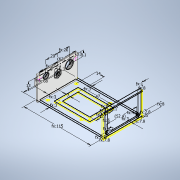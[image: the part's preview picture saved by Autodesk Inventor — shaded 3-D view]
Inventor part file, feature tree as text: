
AUTODESK INVENTOR PART (.ipt)
format: ipt  version: 2022 (Build 260153000, 153)  size: 863,744 bytes
history: native  units: mm
features: extrude x19, sketch x19, fillet x6, plane x4, projected_geometry x4, other x3, revolve x3, pattern_linear x1, mirror x1
ambient origin geometry x8: Origin, YZ Plane, XZ Plane, XY Plane, X Axis, Y Axis, Z Axis, Center Point
bodies: Solid1 (feature_tree)
feature tree (60):
  other  "pi_base_plane"
  extrude  "Extrusion1"  Depth=68.0mm
  extrude  "Extrusion2"  Depth=3.0mm
  other  "pi_outline"
  sketch  "Sketch4"  dims[d2=3.0mm d3=3.0mm]
  extrude  "Extrusion3"  Depth=3.0mm
  sketch  "Sketch5"  dims[d4=3.0mm d5=3.0mm]
  plane  "Work Plane1"
  revolve  "Revolution1"  [1 undecoded]
  sketch  "Sketch Driven Pattern1"  dims[d0=115.0mm d1=68.0mm]
  other  "door"
  extrude  "door_cut"  TaperAngle=0.0deg  [1 undecoded]
  extrude  "Extrusion5"  Depth=85.0mm
  sketch  "Sketch8"  dims[d8=38.0mm d9=0.0mm]
  plane  "Work Plane2"
  extrude  "Extrusion6"  Depth=3.5mm
  revolve  "Revolution2"  [1 undecoded]
  plane  "Work Plane3"
  revolve  "Revolution3"  [1 undecoded]
  fillet  "Fillet1"  Radius=2.7mm
  fillet  "Fillet2"  Radius=3.5mm
  extrude  "Extrusion7"  Depth=2.7mm
  extrude  "M2.5 Side Fastners"  Depth=58.0mm
  sketch  "Sketch14"  dims[d20=58.0mm d21=2.7mm]
  extrude  "Connector and Mount Holes"  Depth=3.0mm
  extrude  "Captive M6 Nut Indent"  Depth=6.5mm
  extrude  "Extrusion12"  Depth=6.5mm
  fillet  "Fillet3"  Radius=6.5mm
  sketch  "Sketch16"  dims[d24=62.0mm d25=3.0mm]
  extrude  "Extrusion13"  TaperAngle=0.0deg  [1 undecoded]
  extrude  "Extrusion14"  Depth=2.1mm
  extrude  "Extrusion15"  TaperAngle=90.0deg  [1 undecoded]
  extrude  "Extrusion16"  Depth=8.0mm
  fillet  "Fillet4"  Radius=8.0mm
  sketch  "Sketch19"  dims[d31=0.4mm d32=0.0mm]
  extrude  "Extrusion17"  Depth=5.0mm
  pattern_linear  "Rectangular Pattern1"  Spacing1=3.0mm  [1 undecoded]
  plane  "Work Plane4"
  mirror  "Mirror1"
  fillet  "Fillet5"  [1 undecoded]
  extrude  "Extrusion18"  Depth=2.0mm TaperAngle=0.0deg
  fillet  "Fillet6"  Radius=4.2mm
  extrude  "Extrusion19"  Depth=7.8mm
  extrude  "Extrusion20"  Depth=7.8mm
  projected_geometry  "Projected Loop1"
  sketch  "Sketch6"  dims[d6=3.0mm d7=0.0mm]
  sketch  "Sketch9"  dims[d10=56.0mm d11=85.0mm]
  sketch  "Sketch10"  dims[d12=2.7mm d13=3.5mm]
  projected_geometry  "Projected Loop2"
  sketch  "Sketch11"  dims[d14=3.5mm d15=2.7mm]
  projected_geometry  "Projected Loop3"
  sketch  "Sketch12"  dims[d16=3.5mm d17=3.5mm d18=2.7mm d19=3.5mm]
  sketch  "Sketch15"  dims[d22=3.5mm d23=58.0mm]
  sketch  "Sketch17"  dims[d26=4.0mm d27=6.5mm]
  sketch  "Sketch18"  dims[d28=6.5mm d29=6.5mm d30=6.5mm]
  projected_geometry  "Projected Loop4"
  sketch  "Sketch20"  dims[d34=4.2mm d35=2.1mm]
  sketch  "Sketch21"  dims[d36=14.3117mm d37=90.0deg]
  sketch  "Sketch22"  dims[d38=8.0mm d39=8.0mm d40=8.0mm]
  sketch  "Sketch23"  dims[d41=5.0mm d42=5.0mm d43=3.0mm d44=0.0mm d45=2.0mm d46=0.0mm d47=4.2mm d48=7.8mm d49=7.8mm d50=4.2mm d51=7.8mm d52=7.8mm d53=3.0mm d54=0.0mm d55=14.3117mm d56=90.0deg d57=52.4mm d58=14.3117mm d59=90.0deg d60=1.0mm d61=1.0mm d62=1.0mm d63=1.0mm d64=0.0mm d65=1.9mm d66=3.0mm d67=0.0mm d70=2.65mm d71=2.65mm d72=20.0mm d73=80.0mm d75=8.0mm d76=0.0mm d77=0.0mm d78=6.3mm d79=9.0mm d80=13.0mm d81=6.0mm d82=9.1mm d84=62.0mm d85=31.0mm d88=0.0mm d89=0.0mm d90=11.0mm d91=2.0mm d92=0.0mm d93=13.0mm d94=20.0mm d95=20.0mm d96=68.0mm d97=58.5mm d98=2.5mm d99=2.5mm d100=2.25mm d101=11.0mm d102=11.0mm d103=6.3mm d104=4.65mm d105=4.65mm d106=5.0mm d107=0.0mm d108=5.0mm d109=47.0mm d110=27.0mm d111=14.0mm d112=11.0mm d113=7.0mm d114=0.0mm d115=0.0mm d116=2.0mm d117=0.0mm d118=3.15mm d119=7.0mm d122=3.15mm d125=3.15mm d128=3.15mm d131=0.0mm d132=0.0mm d133=1.5mm d134=1.0mm d135=0.0mm d136=0.5mm d137=11.0mm d138=5.5mm d139=13.0mm d140=4.0mm d141=1.1mm d142=0.0mm d143=20.0mm d145=80.0mm d146=1.0mm d147=31.0mm d148=31.0mm d149=51.0mm d150=0.0mm d151=15.5mm d152=25.5mm d153=6.0mm d154=37.0mm d155=57.0mm d156=25.0mm d157=20.0mm d158=1.1mm d159=0.0mm d160=2.0mm d161=0.0mm d162=0.0mm d163=0.0mm d164=1.0mm d165=0.0mm]
note: 8 required parameter values undecoded (feature->parameter linkage not recoverable at this tier; creation-order binding heuristic only, values carry confidence <= 0.55)